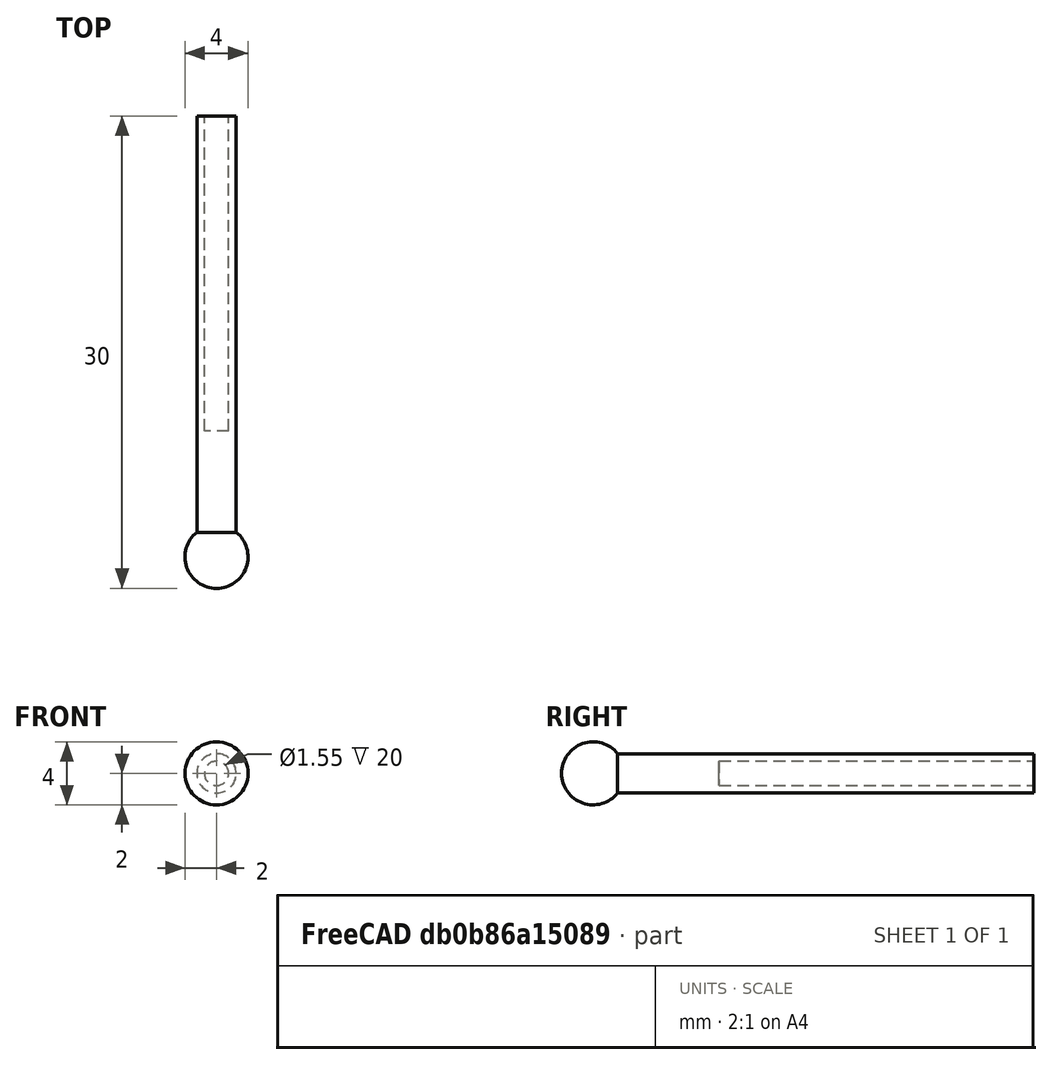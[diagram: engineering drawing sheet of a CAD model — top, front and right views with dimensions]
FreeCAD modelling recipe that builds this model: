
FCSTD DOCUMENT  (FreeCAD 0.19R24366 (Git))
Label: actuator_base
License: All rights reserved
LicenseURL: http://en.wikipedia.org/wiki/All_rights_reserved
objects: Spreadsheet::Sheet×1, Sketcher::SketchObject×1, PartDesign::Revolution×1, PartDesign::Body×1, Mesh::Feature×1
note: 4 computed .brp shape members not serialized (recipe doc carries the construction recipe); baked Part::Feature solids carry a one-line shape summary decoded from their .brp

FEATURE [Spreadsheet::Sheet] Spreadsheet
  cells = A1=BallDiameter; B1(BallDiameter)==4mm; A2=RodDiameter; B2(RodDiameter)==2.5mm; A3=HoleDiameter; B3(HoleDiameter)==1.55mm; A4=HoleDepth; B4(HoleDepth)==20mm; A5=RodLength; B5(RodLength)==30mm
FEATURE [Sketcher::SketchObject] Sketch
  FullyConstrained = true
  MapMode = 5
  Support = -> [XY_Plane]
  expr: Constraints[16] = Spreadsheet.RodLength
  expr: Constraints[15] = 0.5 * Spreadsheet.HoleDiameter
  expr: Constraints[17] = Spreadsheet.HoleDepth
  expr: Constraints[14] = 0.5 * Spreadsheet.RodDiameter
  expr: Constraints[13] = 0.5 * Spreadsheet.BallDiameter
  sketch-geometry (6):
    g0: LineSegment StartX=0 StartY=10 StartZ=0 EndX=0 EndY=0 EndZ=0
    g1: ArcOfCircle CenterX=0 CenterY=2 CenterZ=0 NormalX=0 NormalY=0 NormalZ=1 AngleXU=0 Radius=2 StartAngle=4.71239 EndAngle=7.17885
    g2: LineSegment StartX=0 StartY=10 StartZ=0 EndX=0.775 EndY=10 EndZ=0
    g3: LineSegment StartX=0.775 StartY=10 StartZ=0 EndX=0.775 EndY=30 EndZ=0
    g4: LineSegment StartX=0.775 StartY=30 StartZ=0 EndX=1.25 EndY=30 EndZ=0
    g5: LineSegment StartX=1.25 StartY=30 StartZ=0 EndX=1.25 EndY=3.56125 EndZ=0
  constraints (18):
    c: Coincident(g-1,g0)
    c: Vertical(g0)
    c: Coincident(g0,g1)
    c: PointOnObject(g1,g0)
    c: Horizontal(g2)
    c: Coincident(g2,g3)
    c: Vertical(g3)
    c: Coincident(g3,g4)
    c: Horizontal(g4)
    c: Coincident(g4,g5)
    c: Vertical(g5)
    c: Coincident(g5,g1)
    c: Coincident(g0,g2)
    c: Radius(g1) = 2
    c: DistanceX(g0,g4) = 1.25
    c: DistanceX(g0,g2) = 0.775
    c: DistanceY(g0,g3) = 30
    c: DistanceY(g2,g3) = 20
FEATURE [PartDesign::Revolution] Revolution
  Angle = 360
  Axis = (0,1,0)
  Base = (0,0,0)
  Profile = -> Sketch
  ReferenceAxis = -> Sketch [V_Axis]
  Reversed = true
FEATURE [PartDesign::Body] Body
  Group = -> [Sketch,Revolution]
  Origin = -> Origin
  Tip = -> Revolution
FEATURE [Mesh::Feature] Mesh  label="Body (Meshed)"
